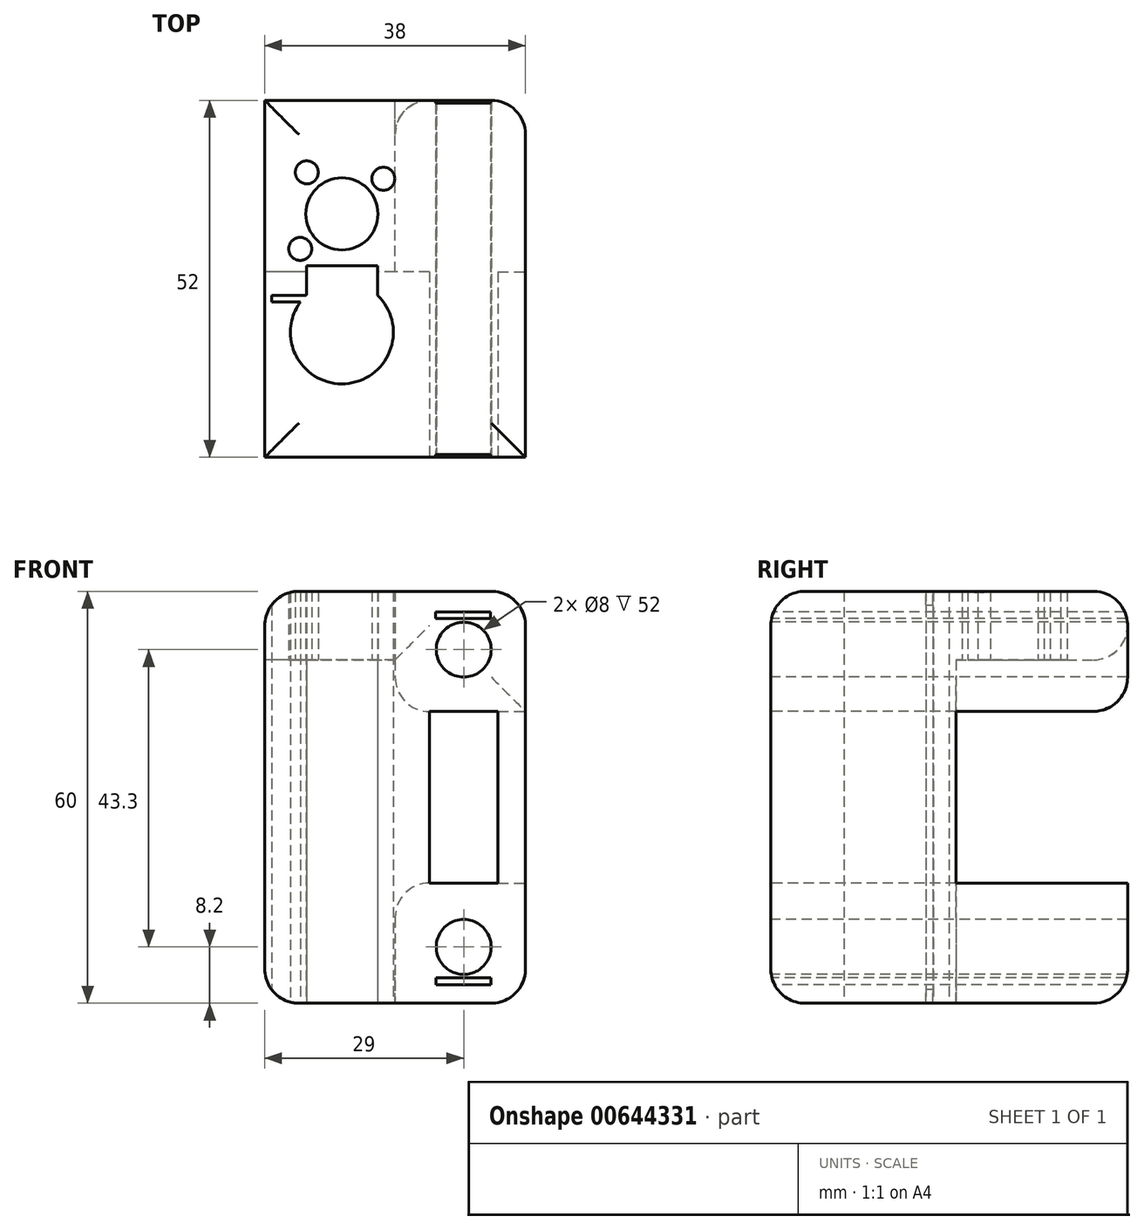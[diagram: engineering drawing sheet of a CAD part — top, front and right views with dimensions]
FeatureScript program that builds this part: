
annotation { "Feature Type Name" : "Feature", "Feature Type Description" : "" }
export const myFeature = defineFeature(function(context is Context, id is Id, definition is map)
    precondition{}
    {
        {
            var Q0;
            Q0=qCreatedBy(makeId("Top.planeOp"),FACE);
            var sketch = newSketch(context, id + "F0", { "sketchPlane" : qUnion([Q0])});
            skLineSegment(sketch, "E0.bottom", {"start": v(19, 26) * mm, "end": v(-19, 26) * mm});
            skLineSegment(sketch, "E0.top", {"start": v(19, -26) * mm, "end": v(-19, -26) * mm});
            skLineSegment(sketch, "E0.left", {"start": v(19, 26) * mm, "end": v(19, -26) * mm});
            skPoint(sketch, "E0.middle", {"position": v(0, 0) * mm});
            skCircle(sketch, "E1", {"center": v(-7.75, 9.45) * mm, "radius": 5.25 * mm});
            skCircle(sketch, "E2", {"center": v(-7.75, -7.8) * mm, "radius": 7.5 * mm});
            skCircle(sketch, "E3", {"center": v(-13.82, 4.36) * mm, "radius": 1.68 * mm});
            skLineSegment(sketch, "E4", {"start": v(-19, 0) * mm, "end": v(11.92, 26) * mm, "construction": true});
            skCircle(sketch, "E5", {"center": v(-1.7, 14.58) * mm, "radius": 1.68 * mm});
            skLineSegment(sketch, "E6", {"start": v(-4.38, 5.42) * mm, "end": v(-19, 22.8) * mm, "construction": true});
            skCircle(sketch, "E7", {"center": v(-12.86, 15.5) * mm, "radius": 1.68 * mm});
            skLineSegment(sketch, "E8.top", {"start": v(-2.55, 0) * mm, "end": v(-12.87, 0) * mm});
            skLineSegment(sketch, "E8.left", {"start": v(-2.55, -2.4) * mm, "end": v(-2.55, 0) * mm});
            skLineSegment(sketch, "E8.right", {"start": v(-12.87, -2.4) * mm, "end": v(-12.87, 0) * mm});
            skLineSegment(sketch, "E9.bottom", {"start": v(-12.87, 0) * mm, "end": v(-2.55, 0) * mm});
            skLineSegment(sketch, "E9.top", {"start": v(-12.87, 1.87) * mm, "end": v(-2.55, 1.87) * mm});
            skLineSegment(sketch, "E9.left", {"start": v(-12.87, 0) * mm, "end": v(-12.87, 1.87) * mm});
            skLineSegment(sketch, "E9.right", {"start": v(-2.55, 0) * mm, "end": v(-2.55, 1.87) * mm});
            skLineSegment(sketch, "E10", {"start": v(-19, 26) * mm, "end": v(-19, -2.4) * mm});
            skLineSegment(sketch, "E11", {"start": v(-19, -3.4) * mm, "end": v(-19, -26) * mm});
            skLineSegment(sketch, "E12.left", {"start": v(-19, -2.4) * mm, "end": v(-19, -3.4) * mm});
            skLineSegment(sketch, "E12.right", {"start": v(-18, -2.4) * mm, "end": v(-18, -3.4) * mm});
            skLineSegment(sketch, "E13", {"start": v(-18, -2.4) * mm, "end": v(-12.87, -2.4) * mm});
            skLineSegment(sketch, "E14", {"start": v(-18, -3.4) * mm, "end": v(-12.87, -3.4) * mm});
            skSolve(sketch);
        }
        {
            var Q0;
            Q0 = qSketchRegion(id + "F0", true);
            extrude(context, id + "F1", {"entities" : qUnion([Q0]), "endBound" : BoundingType.SYMMETRIC, "depth" : 60 * mm, "offsetDistance" : 25 * mm});
        }
        {
            var Q0;
            Q0 = qSketchRegion(id + "F0", true);
            extrude(context, id + "F2", {"entities" : qUnion([Q0]), "operationType" : NewBodyOperationType.ADD, "endBound" : BoundingType.SYMMETRIC, "depth" : 60 * mm, "offsetDistance" : 25 * mm});
        }
        {
            var Q0;
            Q0=makeQuery(id+"F1.opExtrude","SWEPT_FACE",FACE,{"disambiguationData":[OSD([sQuery(id+"F0.wireOp",EDGE,"E0.top")])]});
            var sketch = newSketch(context, id + "F3", { "sketchPlane" : qUnion([Q0])});
            skCircle(sketch, "E15", {"center": v(10, 21.5) * mm, "radius": 4 * mm});
            skCircle(sketch, "E16", {"center": v(10, -21.8) * mm, "radius": 4 * mm});
            skLineSegment(sketch, "E17.bottom", {"start": v(5, 12.5) * mm, "end": v(15, 12.5) * mm});
            skLineSegment(sketch, "E17.top", {"start": v(5, -12.5) * mm, "end": v(15, -12.5) * mm});
            skLineSegment(sketch, "E17.left", {"start": v(5, 12.5) * mm, "end": v(5, -12.5) * mm});
            skLineSegment(sketch, "E17.right", {"start": v(15, 12.5) * mm, "end": v(15, -12.5) * mm});
            skPoint(sketch, "E17.middle", {"position": v(10, 0) * mm});
            skLineSegment(sketch, "E18.bottom", {"start": v(5.88, 27) * mm, "end": v(13.88, 27) * mm});
            skLineSegment(sketch, "E18.top", {"start": v(5.88, 26) * mm, "end": v(13.88, 26) * mm});
            skLineSegment(sketch, "E18.left", {"start": v(5.88, 27) * mm, "end": v(5.88, 26) * mm});
            skLineSegment(sketch, "E18.right", {"start": v(13.88, 27) * mm, "end": v(13.88, 26) * mm});
            skLineSegment(sketch, "E19.bottom", {"start": v(5.98, -26.3) * mm, "end": v(13.98, -26.3) * mm});
            skLineSegment(sketch, "E19.top", {"start": v(5.98, -27.3) * mm, "end": v(13.98, -27.3) * mm});
            skLineSegment(sketch, "E19.left", {"start": v(5.98, -26.3) * mm, "end": v(5.98, -27.3) * mm});
            skLineSegment(sketch, "E19.right", {"start": v(13.98, -26.3) * mm, "end": v(13.98, -27.3) * mm});
            skSolve(sketch);
        }
        {
            var Q0;
            Q0 = qSketchRegion(id + "F3", true);
            extrude(context, id + "F4", {"entities" : qUnion([Q0]), "operationType" : NewBodyOperationType.REMOVE, "endBound" : BoundingType.THROUGH_ALL, "oppositeDirection" : true, "depth" : 52 * mm, "offsetDistance" : 25 * mm});
        }
        {
            var Q0;
            Q0=makeQuery(id+"F1.opExtrude","SWEPT_FACE",FACE,{"disambiguationData":[OSD([sQuery(id+"F0.wireOp",EDGE,"E0.bottom")])]});
            var sketch = newSketch(context, id + "F5", { "sketchPlane" : qUnion([Q0])});
            skLineSegment(sketch, "E20.bottom", {"start": v(0, 20) * mm, "end": v(19, 20) * mm});
            skLineSegment(sketch, "E20.top", {"start": v(0, -30) * mm, "end": v(19, -30) * mm});
            skLineSegment(sketch, "E20.left", {"start": v(0, 20) * mm, "end": v(0, -30) * mm});
            skLineSegment(sketch, "E20.right", {"start": v(19, 20) * mm, "end": v(19, -30) * mm});
            skLineSegment(sketch, "E21.bottom", {"start": v(0, 12.5) * mm, "end": v(-19, 12.5) * mm});
            skLineSegment(sketch, "E21.top", {"start": v(0, -12.5) * mm, "end": v(-19, -12.5) * mm});
            skLineSegment(sketch, "E21.left", {"start": v(0, 12.5) * mm, "end": v(0, -12.5) * mm});
            skLineSegment(sketch, "E21.right", {"start": v(-19, 12.5) * mm, "end": v(-19, -12.5) * mm});
            skSolve(sketch);
        }
        {
            var Q0;
            Q0 = qSketchRegion(id + "F5", true);
            extrude(context, id + "F6", {"entities" : qUnion([Q0]), "operationType" : NewBodyOperationType.REMOVE, "oppositeDirection" : true, "depth" : 25 * mm, "offsetDistance" : 25 * mm});
        }
        {
            var Q0;
            Q0=makeQuery(id+"F6.boolean.opBoolean","COPY",EDGE,{"derivedFrom":makeQuery(id+"F6.opExtrude","SWEPT_EDGE",EDGE,{"disambiguationData":[OSD([sQuery(id+"F0.wireOp",EDGE,"E0.bottom"),sQuery(id+"F5.wireOp",EDGE,"E20.top"),sQuery(id+"F5.wireOp",EDGE,"E20.left")])]})});
            var Q1;
            {var subQ0=sQuery(id+"F5.wireOp",EDGE,"E20.left");Q1=makeQuery(id+"F6.boolean.opBoolean","COPY",EDGE,{"derivedFrom":makeQuery(id+"F6.opExtrude","CAP_EDGE",EDGE,{"disambiguationData":[OSD([subQ0]),TDD([makeQuery(id+"F5.imprint","IMPRINT",EDGE,{"disambiguationData":[TD([[makeQuery(id+"F5.imprint","INTERSECT",VERTEX,{"derivedFrom":[sQuery(id+"F5.wireOp",EDGE,"E20.bottom"),subQ0]}),-1.0]])],"derivedFrom":subQ0})])],"isStart":true})});}
            var Q2;
            {var subQ0=sQuery(id+"F5.wireOp",EDGE,"E20.left");Q2=makeQuery(id+"F6.boolean.opBoolean","COPY",EDGE,{"derivedFrom":makeQuery(id+"F6.opExtrude","CAP_EDGE",EDGE,{"disambiguationData":[OSD([subQ0]),TDD([makeQuery(id+"F5.imprint","IMPRINT",EDGE,{"disambiguationData":[TD([[makeQuery(id+"F5.imprint","INTERSECT",VERTEX,{"derivedFrom":[makeQuery(id+"F1.opExtrude","CAP_EDGE",EDGE,{"disambiguationData":[OSD([sQuery(id+"F0.wireOp",EDGE,"E0.bottom")])],"isStart":true}),sQuery(id+"F5.wireOp",EDGE,"E20.top"),subQ0]}),1.0]])],"derivedFrom":subQ0})])],"isStart":true})});}
            var Q3;
            Q3=makeQuery(id+"F6.boolean.opBoolean","COPY",EDGE,{"derivedFrom":makeQuery(id+"F6.opExtrude","CAP_EDGE",EDGE,{"disambiguationData":[OSD([sQuery(id+"F5.wireOp",EDGE,"E20.right")])],"isStart":false})});
            var Q4;
            Q4=makeQuery(id+"F6.boolean.opBoolean","COPY",EDGE,{"derivedFrom":makeQuery(id+"F6.opExtrude","SWEPT_EDGE",EDGE,{"disambiguationData":[OSD([sQuery(id+"F0.wireOp",EDGE,"E0.bottom"),sQuery(id+"F0.wireOp",EDGE,"E0.left"),sQuery(id+"F5.wireOp",EDGE,"E21.top"),sQuery(id+"F5.wireOp",EDGE,"E21.right")])]})});
            var Q5;
            Q5=makeQuery(id+"F6.boolean.opBoolean","COPY",EDGE,{"derivedFrom":makeQuery(id+"F6.opExtrude","SWEPT_EDGE",EDGE,{"disambiguationData":[OSD([sQuery(id+"F5.wireOp",EDGE,"E20.left"),sQuery(id+"F5.wireOp",EDGE,"E21.top"),sQuery(id+"F5.wireOp",EDGE,"E21.left")])]})});
            var Q6;
            Q6=makeQuery(id+"F1.opExtrude","CAP_EDGE",EDGE,{"disambiguationData":[OSD([sQuery(id+"F0.wireOp",EDGE,"E0.left")])],"isStart":true});
            var Q7;
            Q7=makeQuery(id+"F1.opExtrude","CAP_EDGE",EDGE,{"disambiguationData":[OSD([sQuery(id+"F0.wireOp",EDGE,"E0.left")])],"isStart":false});
            var Q8;
            Q8=makeQuery(id+"F6.boolean.opBoolean","COPY",EDGE,{"derivedFrom":makeQuery(id+"F6.opExtrude","CAP_EDGE",EDGE,{"disambiguationData":[OSD([sQuery(id+"F5.wireOp",EDGE,"E21.right")])],"isStart":false})});
            var Q9;
            Q9=makeQuery(id+"F6.boolean.opBoolean","COPY",EDGE,{"derivedFrom":makeQuery(id+"F6.opExtrude","SWEPT_EDGE",EDGE,{"disambiguationData":[OSD([sQuery(id+"F5.wireOp",EDGE,"E20.left"),sQuery(id+"F5.wireOp",EDGE,"E21.bottom"),sQuery(id+"F5.wireOp",EDGE,"E21.left")])]})});
            var Q10;
            Q10=makeQuery(id+"F6.boolean.opBoolean","MERGE",EDGE,{"derivedFrom":[makeQuery(id+"F4.boolean.opBoolean","INTERSECT",EDGE,{"derivedFrom":[makeQuery(id+"F1.opExtrude","SWEPT_FACE",FACE,{"disambiguationData":[OSD([sQuery(id+"F0.wireOp",EDGE,"E0.bottom")])]}),makeQuery(id+"F4.opExtrude","SWEPT_FACE",FACE,{"disambiguationData":[OSD([sQuery(id+"F3.wireOp",EDGE,"E17.bottom")])]})]}),makeQuery(id+"F6.opExtrude","CAP_EDGE",EDGE,{"disambiguationData":[OSD([sQuery(id+"F5.wireOp",EDGE,"E21.bottom")])],"isStart":true})]});
            var Q11;
            Q11=makeQuery(id+"F6.boolean.opBoolean","MERGE",EDGE,{"derivedFrom":[makeQuery(id+"F4.boolean.opBoolean","INTERSECT",EDGE,{"derivedFrom":[makeQuery(id+"F1.opExtrude","SWEPT_FACE",FACE,{"disambiguationData":[OSD([sQuery(id+"F0.wireOp",EDGE,"E0.bottom")])]}),makeQuery(id+"F4.opExtrude","SWEPT_FACE",FACE,{"disambiguationData":[OSD([sQuery(id+"F3.wireOp",EDGE,"E17.top")])]})]}),makeQuery(id+"F6.opExtrude","CAP_EDGE",EDGE,{"disambiguationData":[OSD([sQuery(id+"F5.wireOp",EDGE,"E21.top")])],"isStart":true})]});
            var Q12;
            {var subQ0=sQuery(id+"F0.wireOp",EDGE,"E0.left");var subQ1=sQuery(id+"F0.wireOp",EDGE,"E0.bottom");Q12=makeQuery(id+"F6.boolean.opBoolean","SPLIT",EDGE,{"disambiguationData":[TD([makeQuery(id+"F4.boolean.opBoolean","COPY",FACE,{"derivedFrom":makeQuery(id+"F4.opExtrude","SWEPT_FACE",FACE,{"disambiguationData":[OSD([sQuery(id+"F3.wireOp",EDGE,"E17.bottom")])]})})])],"derivedFrom":makeQuery(id+"F1.opExtrude","SWEPT_EDGE",EDGE,{"disambiguationData":[OSD([subQ1,subQ0])]})});}
            var Q13;
            {var subQ0=sQuery(id+"F0.wireOp",EDGE,"E0.left");var subQ1=sQuery(id+"F0.wireOp",EDGE,"E0.bottom");Q13=makeQuery(id+"F6.boolean.opBoolean","SPLIT",EDGE,{"disambiguationData":[TD([makeQuery(id+"F4.boolean.opBoolean","COPY",FACE,{"derivedFrom":makeQuery(id+"F4.opExtrude","SWEPT_FACE",FACE,{"disambiguationData":[OSD([sQuery(id+"F3.wireOp",EDGE,"E17.top")])]})})])],"derivedFrom":makeQuery(id+"F1.opExtrude","SWEPT_EDGE",EDGE,{"disambiguationData":[OSD([subQ1,subQ0])]})});}
            var Q14;
            Q14=makeQuery(id+"F1.opExtrude","CAP_EDGE",EDGE,{"disambiguationData":[OSD([sQuery(id+"F0.wireOp",EDGE,"E0.bottom")])],"isStart":false});
            var Q15;
            Q15=makeQuery(id+"F1.opExtrude","CAP_EDGE",EDGE,{"disambiguationData":[OSD([sQuery(id+"F0.wireOp",EDGE,"E0.bottom")])],"isStart":true});
            var Q16;
            Q16=makeQuery(id+"F1.opExtrude","CAP_EDGE",EDGE,{"disambiguationData":[OSD([sQuery(id+"F0.wireOp",EDGE,"E0.top")])],"isStart":true});
            var Q17;
            Q17=makeQuery(id+"F1.opExtrude","CAP_EDGE",EDGE,{"disambiguationData":[OSD([sQuery(id+"F0.wireOp",EDGE,"E10"),sQuery(id+"F0.wireOp",EDGE,"E11"),sQuery(id+"F0.wireOp",EDGE,"E12.left")])],"isStart":true});
            var Q18;
            Q18=makeQuery(id+"F1.opExtrude","CAP_EDGE",EDGE,{"disambiguationData":[OSD([sQuery(id+"F0.wireOp",EDGE,"E0.top")])],"isStart":false});
            var Q19;
            Q19=makeQuery(id+"F1.opExtrude","CAP_EDGE",EDGE,{"disambiguationData":[OSD([sQuery(id+"F0.wireOp",EDGE,"E10"),sQuery(id+"F0.wireOp",EDGE,"E11"),sQuery(id+"F0.wireOp",EDGE,"E12.left")])],"isStart":false});
            var Q20;
            Q20=makeQuery(id+"F6.boolean.opBoolean","COPY",EDGE,{"derivedFrom":makeQuery(id+"F6.opExtrude","SWEPT_EDGE",EDGE,{"disambiguationData":[OSD([sQuery(id+"F0.wireOp",EDGE,"E0.bottom"),sQuery(id+"F0.wireOp",EDGE,"E10"),sQuery(id+"F5.wireOp",EDGE,"E20.bottom"),sQuery(id+"F5.wireOp",EDGE,"E20.right")])]})});
            var Q21;
            Q21=makeQuery(id+"F6.boolean.opBoolean","COPY",EDGE,{"derivedFrom":makeQuery(id+"F6.opExtrude","CAP_EDGE",EDGE,{"disambiguationData":[OSD([sQuery(id+"F5.wireOp",EDGE,"E20.bottom")])],"isStart":true})});
            var Q22;
            Q22=makeQuery(id+"F6.boolean.opBoolean","COPY",EDGE,{"derivedFrom":makeQuery(id+"F6.opExtrude","SWEPT_EDGE",EDGE,{"disambiguationData":[OSD([sQuery(id+"F0.wireOp",EDGE,"E0.bottom"),sQuery(id+"F0.wireOp",EDGE,"E0.left"),sQuery(id+"F5.wireOp",EDGE,"E21.bottom"),sQuery(id+"F5.wireOp",EDGE,"E21.right")])]})});
            fillet(context, id + "F7", {"entities" : qUnion([Q0, Q1, Q2, Q3, Q4, Q5, Q6, Q7, Q8, Q9, Q10, Q11, Q12, Q13, Q14, Q15, Q16, Q17, Q18, Q19, Q20, Q21, Q22]), "radius" : 5 * mm, "tangentPropagation" : true, "allowEdgeOverflow" : false});
        }
    });
